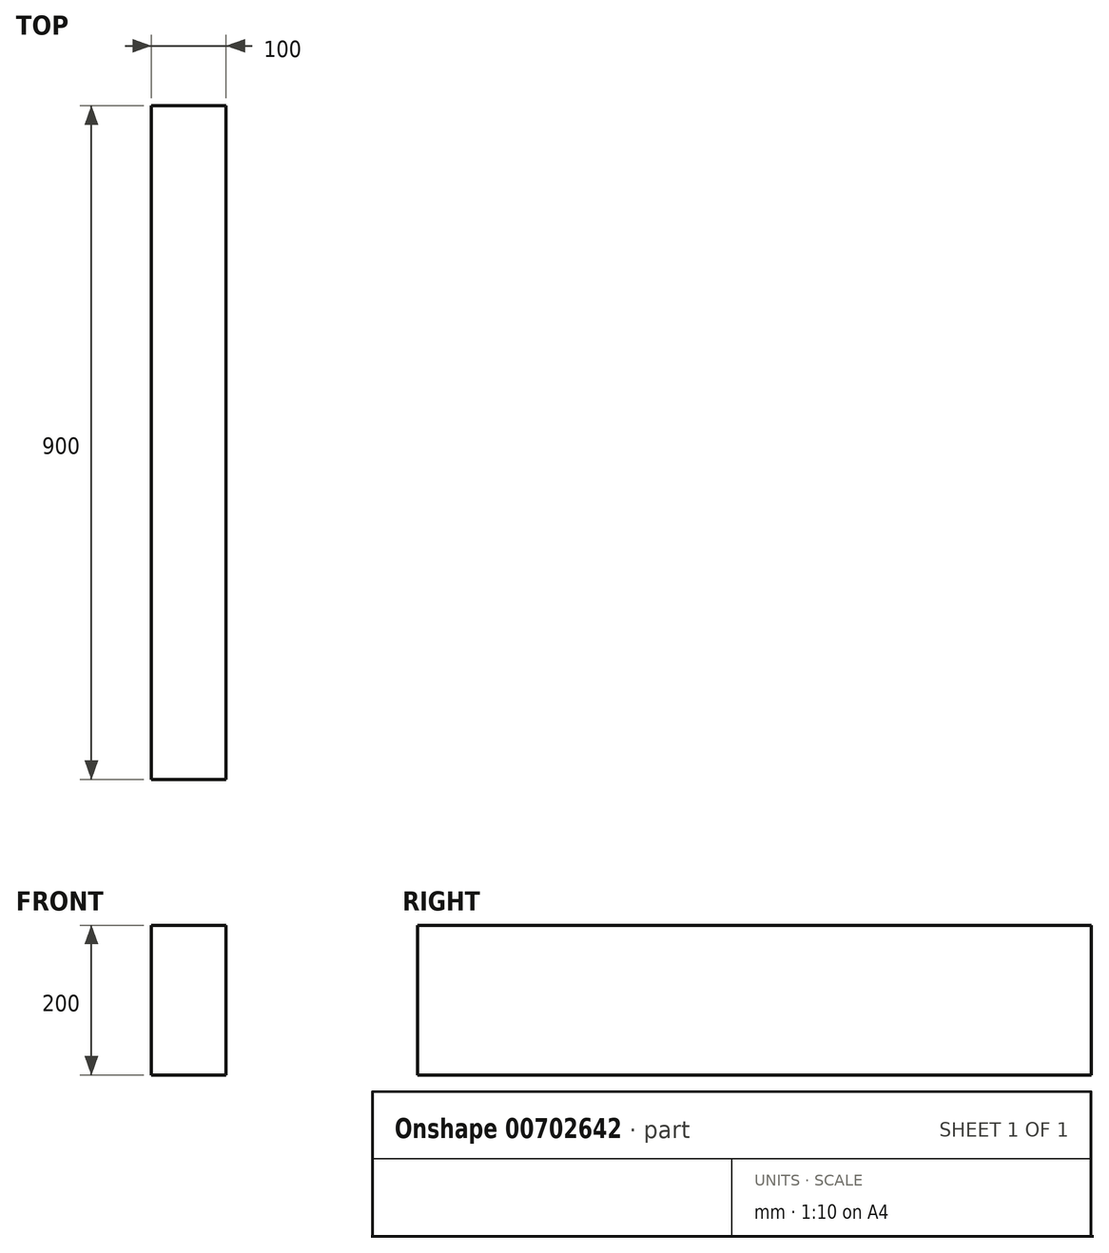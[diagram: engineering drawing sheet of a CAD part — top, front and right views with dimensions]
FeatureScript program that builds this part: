
annotation { "Feature Type Name" : "Feature", "Feature Type Description" : "" }
export const myFeature = defineFeature(function(context is Context, id is Id, definition is map)
    precondition{}
    {
        {
            var Q0;
            Q0=qCreatedBy(makeId("Front.planeOp"),FACE);
            var sketch = newSketch(context, id + "F0", { "sketchPlane" : qUnion([Q0])});
            skLineSegment(sketch, "E0.bottom", {"start": v(0, 0) * mm, "end": v(-100, 0) * mm});
            skLineSegment(sketch, "E0.top", {"start": v(0, 200) * mm, "end": v(-100, 200) * mm});
            skLineSegment(sketch, "E0.left", {"start": v(0, 0) * mm, "end": v(0, 200) * mm});
            skLineSegment(sketch, "E0.right", {"start": v(-100, 0) * mm, "end": v(-100, 200) * mm});
            skSolve(sketch);
        }
        {
            var Q0;
            Q0=qSketchRegion(id+"F0",true);
            extrude(context, id + "F1", {"entities" : qUnion([Q0]), "depth" : 900 * mm, "offsetDistance" : 25 * mm});
        }
    });
